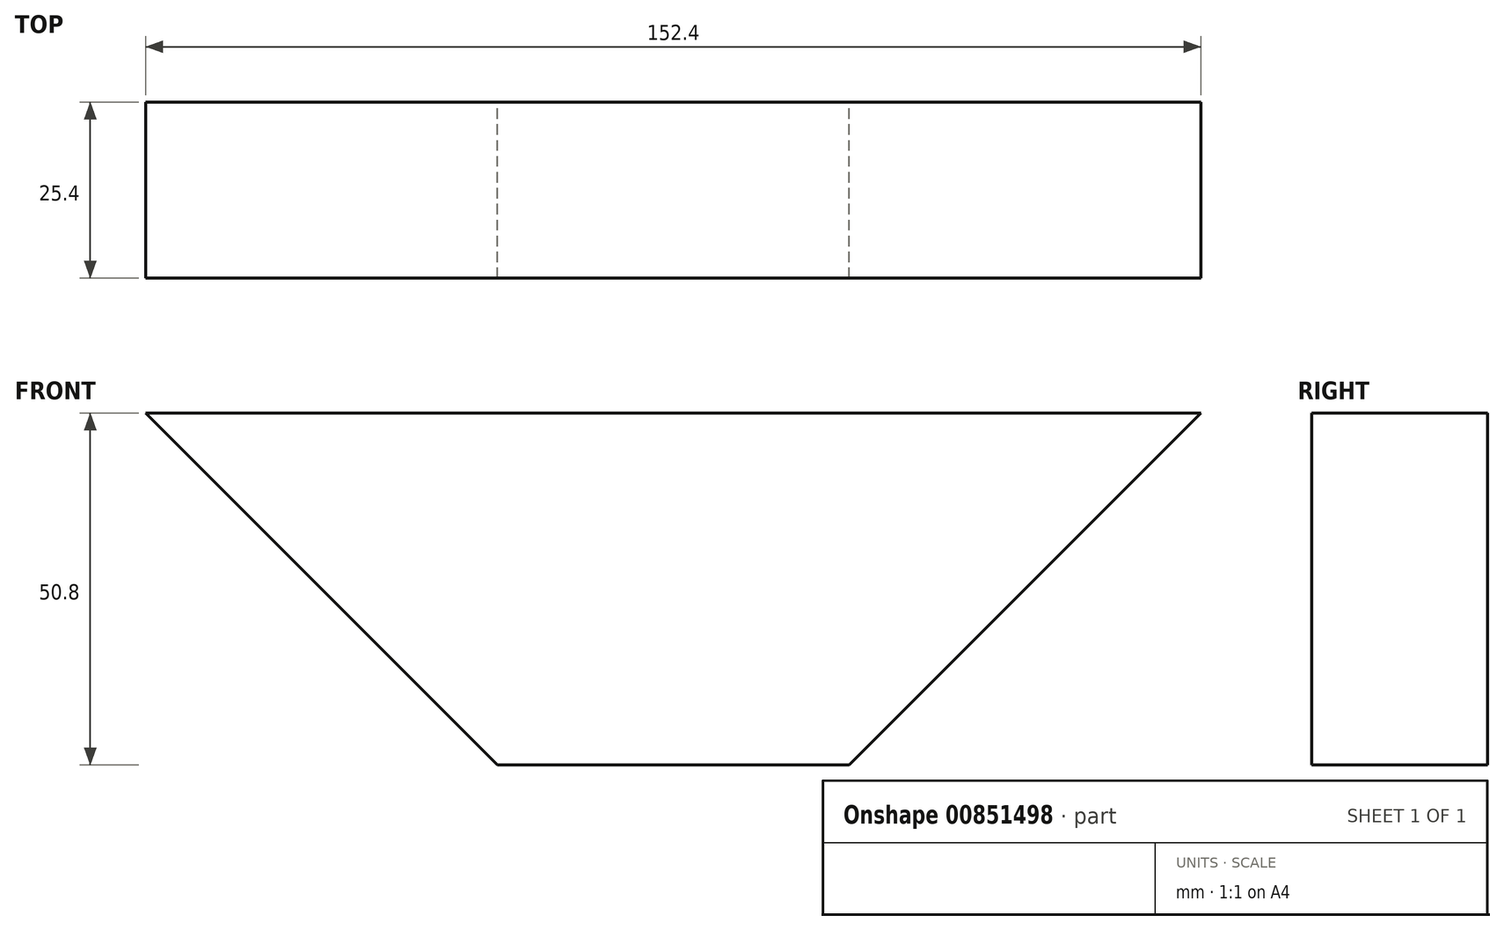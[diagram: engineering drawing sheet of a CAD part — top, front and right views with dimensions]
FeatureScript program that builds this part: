
annotation { "Feature Type Name" : "Feature", "Feature Type Description" : "" }
export const myFeature = defineFeature(function(context is Context, id is Id, definition is map)
    precondition{}
    {
        {
            var Q0;
            Q0=qCreatedBy(makeId("Front.planeOp"),FACE);
            var sketch = newSketch(context, id + "F0", { "sketchPlane" : qUnion([Q0])});
            skLineSegment(sketch, "E0.bottom", {"start": v(-106.66, 50.8) * mm, "end": v(45.74, 50.8) * mm});
            skLineSegment(sketch, "E0.top", {"start": v(-55.86, 0) * mm, "end": v(-5.06, 0) * mm});
            skLineSegment(sketch, "E1", {"start": v(45.74, 50.8) * mm, "end": v(-5.06, 0) * mm});
            skLineSegment(sketch, "E2", {"start": v(-106.66, 50.8) * mm, "end": v(-55.86, 0) * mm});
            skPoint(sketch, "E3.orphan", {"position": v(45.74, 0) * mm});
            skSolve(sketch);
        }
        {
            var Q0;
            Q0 = qSketchRegion(id + "F0", true);
            extrude(context, id + "F1", {"entities" : qUnion([Q0]), "depth" : 25.4 * mm, "offsetDistance" : 25.4 * mm});
        }
    });
